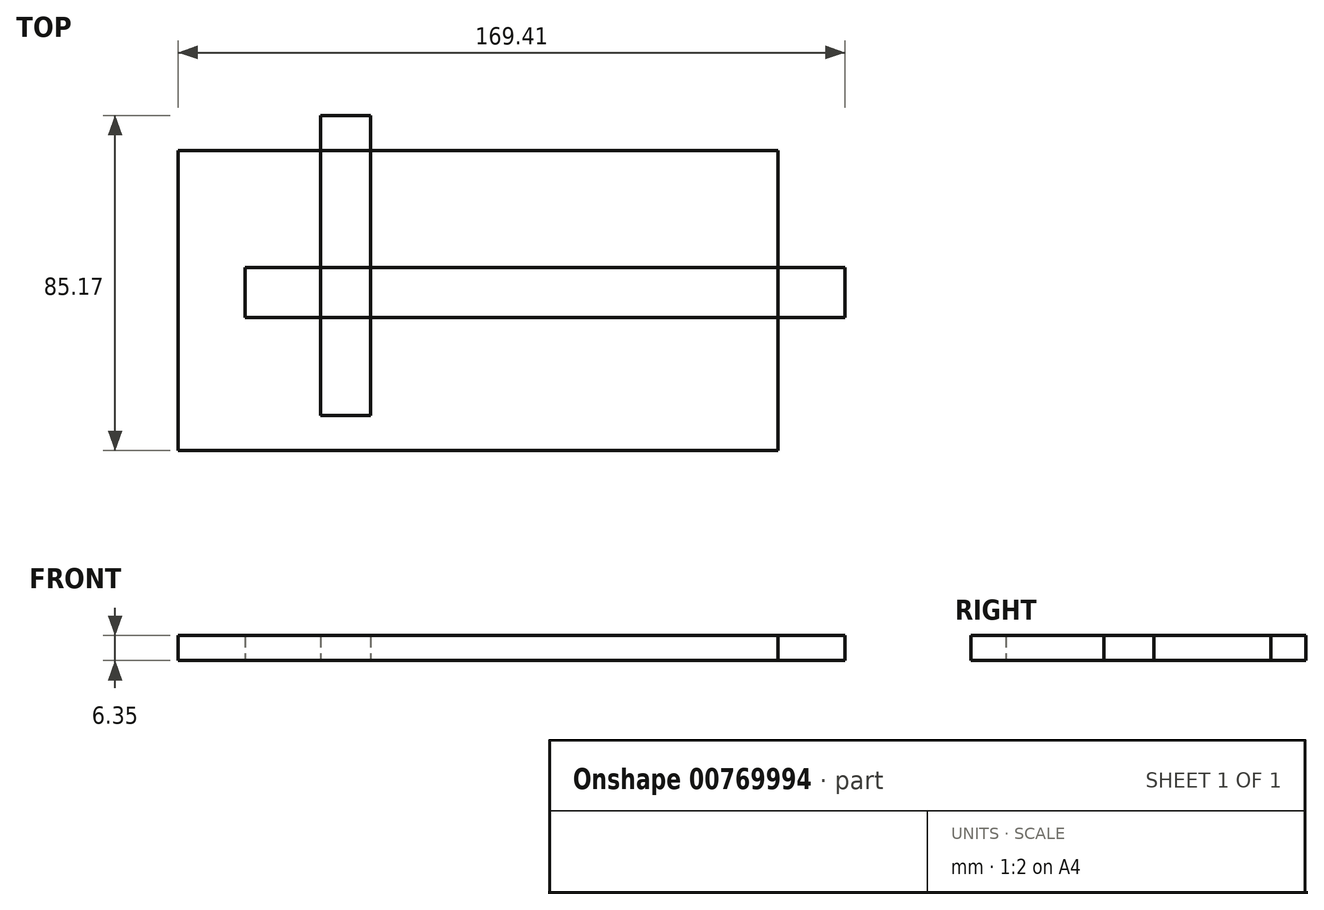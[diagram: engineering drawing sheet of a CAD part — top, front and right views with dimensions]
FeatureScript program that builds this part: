
annotation { "Feature Type Name" : "Feature", "Feature Type Description" : "" }
export const myFeature = defineFeature(function(context is Context, id is Id, definition is map)
    precondition{}
    {
        {
            var Q0;
            Q0=qCreatedBy(makeId("Top.planeOp"),FACE);
            var sketch = newSketch(context, id + "F0", { "sketchPlane" : qUnion([Q0])});
            skLineSegment(sketch, "E0.bottom", {"start": v(-87.6, 70.09) * mm, "end": v(64.8, 70.09) * mm});
            skLineSegment(sketch, "E0.top", {"start": v(-87.6, -6.11) * mm, "end": v(64.8, -6.11) * mm});
            skLineSegment(sketch, "E0.left", {"start": v(-87.6, 70.09) * mm, "end": v(-87.6, -6.11) * mm});
            skLineSegment(sketch, "E0.right", {"start": v(64.8, 70.09) * mm, "end": v(64.8, -6.11) * mm});
            skSolve(sketch);
        }
        {
            var Q0;
            Q0=makeQuery(id+"F0.imprint","IMPRINT",FACE,{"disambiguationData":[TD([[makeQuery(id+"F0.imprint","IMPRINT",EDGE,{"derivedFrom":sQuery(id+"F0.wireOp",EDGE,"E0.bottom")}),-1.0]])]});
            extrude(context, id + "F1", {"entities" : qUnion([Q0]), "depth" : 6.35 * mm, "offsetDistance" : 25.4 * mm});
        }
        {
            var Q0;
            Q0=qCreatedBy(makeId("Top.planeOp"),FACE);
            var sketch = newSketch(context, id + "F2", { "sketchPlane" : qUnion([Q0])});
            skLineSegment(sketch, "E1.bottom", {"start": v(-70.59, 40.42) * mm, "end": v(81.81, 40.42) * mm});
            skLineSegment(sketch, "E1.top", {"start": v(-70.59, 27.72) * mm, "end": v(81.81, 27.72) * mm});
            skLineSegment(sketch, "E1.left", {"start": v(-70.59, 40.42) * mm, "end": v(-70.59, 27.72) * mm});
            skLineSegment(sketch, "E1.right", {"start": v(81.81, 40.42) * mm, "end": v(81.81, 27.72) * mm});
            skSolve(sketch);
        }
        {
            var Q0;
            Q0=makeQuery(id+"F2.imprint","IMPRINT",FACE,{"disambiguationData":[TD([[makeQuery(id+"F2.imprint","IMPRINT",EDGE,{"derivedFrom":sQuery(id+"F2.wireOp",EDGE,"E1.bottom")}),-1.0]])]});
            extrude(context, id + "F3", {"entities" : qUnion([Q0]), "depth" : 6.35 * mm, "offsetDistance" : 25.4 * mm});
        }
        {
            var Q0;
            Q0=qCreatedBy(makeId("Top.planeOp"),FACE);
            var sketch = newSketch(context, id + "F4", { "sketchPlane" : qUnion([Q0])});
            skLineSegment(sketch, "E2.bottom", {"start": v(-51.44, 79.06) * mm, "end": v(-38.74, 79.06) * mm});
            skLineSegment(sketch, "E2.top", {"start": v(-51.44, 2.86) * mm, "end": v(-38.74, 2.86) * mm});
            skLineSegment(sketch, "E2.left", {"start": v(-51.44, 79.06) * mm, "end": v(-51.44, 2.86) * mm});
            skLineSegment(sketch, "E2.right", {"start": v(-38.74, 79.06) * mm, "end": v(-38.74, 2.86) * mm});
            skLineSegment(sketch, "E3.bottom", {"start": v(-51.44, 79.06) * mm, "end": v(-51.44, 79.06) * mm});
            skLineSegment(sketch, "E3.top", {"start": v(-51.44, 2.86) * mm, "end": v(-51.44, 2.86) * mm});
            skSolve(sketch);
        }
        {
            var Q0;
            Q0=makeQuery(id+"F4.imprint","IMPRINT",FACE,{"disambiguationData":[TD([[makeQuery(id+"F4.imprint","IMPRINT",EDGE,{"derivedFrom":sQuery(id+"F4.wireOp",EDGE,"E2.bottom")}),-1.0]])]});
            extrude(context, id + "F5", {"entities" : qUnion([Q0]), "depth" : 6.35 * mm, "offsetDistance" : 25.4 * mm});
        }
    });
